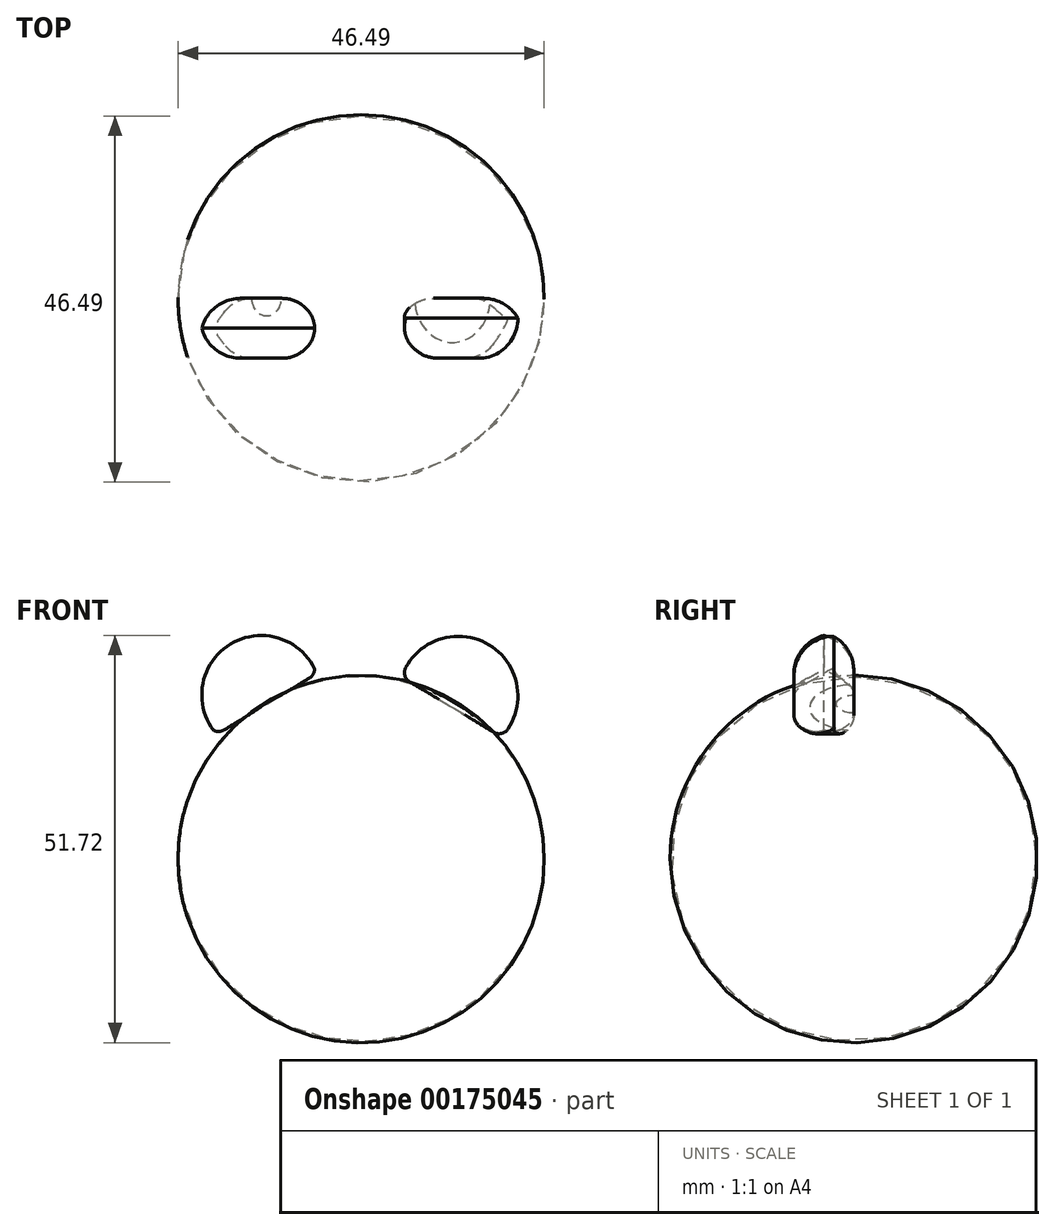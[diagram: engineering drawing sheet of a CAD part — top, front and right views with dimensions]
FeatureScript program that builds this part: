
annotation { "Feature Type Name" : "Feature", "Feature Type Description" : "" }
export const myFeature = defineFeature(function(context is Context, id is Id, definition is map)
    precondition{}
    {
        {
            var Q0;
            Q0=qCreatedBy(makeId("Front.planeOp"),FACE);
            var sketch = newSketch(context, id + "F0", { "sketchPlane" : qUnion([Q0])});
            skLineSegment(sketch, "E0", {"start": v(-76.37, 0) * mm, "end": v(0, 0) * mm});
            skArc(sketch, "E1", {"start": v(-16.45, 0) * mm, "mid": v(-39.7, 23.15) * mm, "end": v(-62.94, 0) * mm});
            skSolve(sketch);
        }
        {
            var Q0;
            Q0 = qSketchRegion(id + "F0", true);
            var Q1;
            Q1=sQuery(id+"F0.wireOp",EDGE,"E0");
            revolve(context, id + "F1", {"entities" : qUnion([Q0]), "axis" : qUnion([Q1]), "revolveType" : RevolveType.FULL});
        }
        {
            var Q0;
            Q0=qCreatedBy(makeId("Front.planeOp"),FACE);
            var sketch = newSketch(context, id + "F2", { "sketchPlane" : qUnion([Q0])});
            skArc(sketch, "E2", {"start": v(-45.81, 24.84) * mm, "mid": v(-56.4, 27.42) * mm, "end": v(-58.97, 16.84) * mm});
            skLineSegment(sketch, "E3", {"start": v(-57.11, 16.39) * mm, "end": v(-46.26, 22.98) * mm});
            skArc(sketch, "E4", {"start": v(-21.03, 16.51) * mm, "mid": v(-23.45, 27.2) * mm, "end": v(-34.03, 24.3) * mm});
            skLineSegment(sketch, "E5", {"start": v(-33.53, 22.5) * mm, "end": v(-22.86, 16.1) * mm});
            skPoint(sketch, "E6.visualSharp", {"position": v(-21.84, 15.5) * mm});
            skArc(sketch, "E6.filletArc", {"start": v(-22.86, 16.1) * mm, "mid": v(-21.86, 15.94) * mm, "end": v(-21.03, 16.51) * mm});
            skPoint(sketch, "E7.visualSharp", {"position": v(-34.54, 23.11) * mm});
            skArc(sketch, "E7.filletArc", {"start": v(-34.03, 24.3) * mm, "mid": v(-34.14, 23.3) * mm, "end": v(-33.53, 22.5) * mm});
            skPoint(sketch, "E8.visualSharp", {"position": v(-58.17, 15.75) * mm});
            skArc(sketch, "E8.filletArc", {"start": v(-58.97, 16.84) * mm, "mid": v(-58.14, 16.23) * mm, "end": v(-57.11, 16.39) * mm});
            skPoint(sketch, "E9.visualSharp", {"position": v(-45.21, 23.62) * mm});
            skArc(sketch, "E9.filletArc", {"start": v(-46.26, 22.98) * mm, "mid": v(-45.65, 23.82) * mm, "end": v(-45.81, 24.84) * mm});
            skSolve(sketch);
        }
        {
            var Q0;
            Q0 = qSketchRegion(id + "F2", true);
            extrude(context, id + "F3", {"entities" : qUnion([Q0]), "operationType" : NewBodyOperationType.ADD, "depth" : 7.62 * mm, "offsetDistance" : 25.4 * mm});
        }
        {
            var Q0;
            Q0=makeQuery(id+"F3.opExtrude","CAP_EDGE",EDGE,{"disambiguationData":[OSD([sQuery(id+"F2.wireOp",EDGE,"E4")])],"isStart":false});
            fillet(context, id + "F4", {"entities" : qUnion([Q0]), "radius" : 5.08 * mm, "allowEdgeOverflow" : false});
        }
        {
            var Q0;
            Q0=makeQuery(id+"F3.opExtrude","CAP_EDGE",EDGE,{"disambiguationData":[OSD([sQuery(id+"F2.wireOp",EDGE,"E2")])],"isStart":false});
            var Q1;
            Q1=makeQuery(id+"F3.opExtrude","CAP_EDGE",EDGE,{"disambiguationData":[OSD([sQuery(id+"F2.wireOp",EDGE,"E2")])],"isStart":true});
            var Q2;
            Q2=makeQuery(id+"F3.opExtrude","CAP_EDGE",EDGE,{"disambiguationData":[OSD([sQuery(id+"F2.wireOp",EDGE,"E4")])],"isStart":true});
            fillet(context, id + "F5", {"entities" : qUnion([Q0, Q1, Q2]), "radius" : 5.08 * mm, "allowEdgeOverflow" : false});
        }
    });
